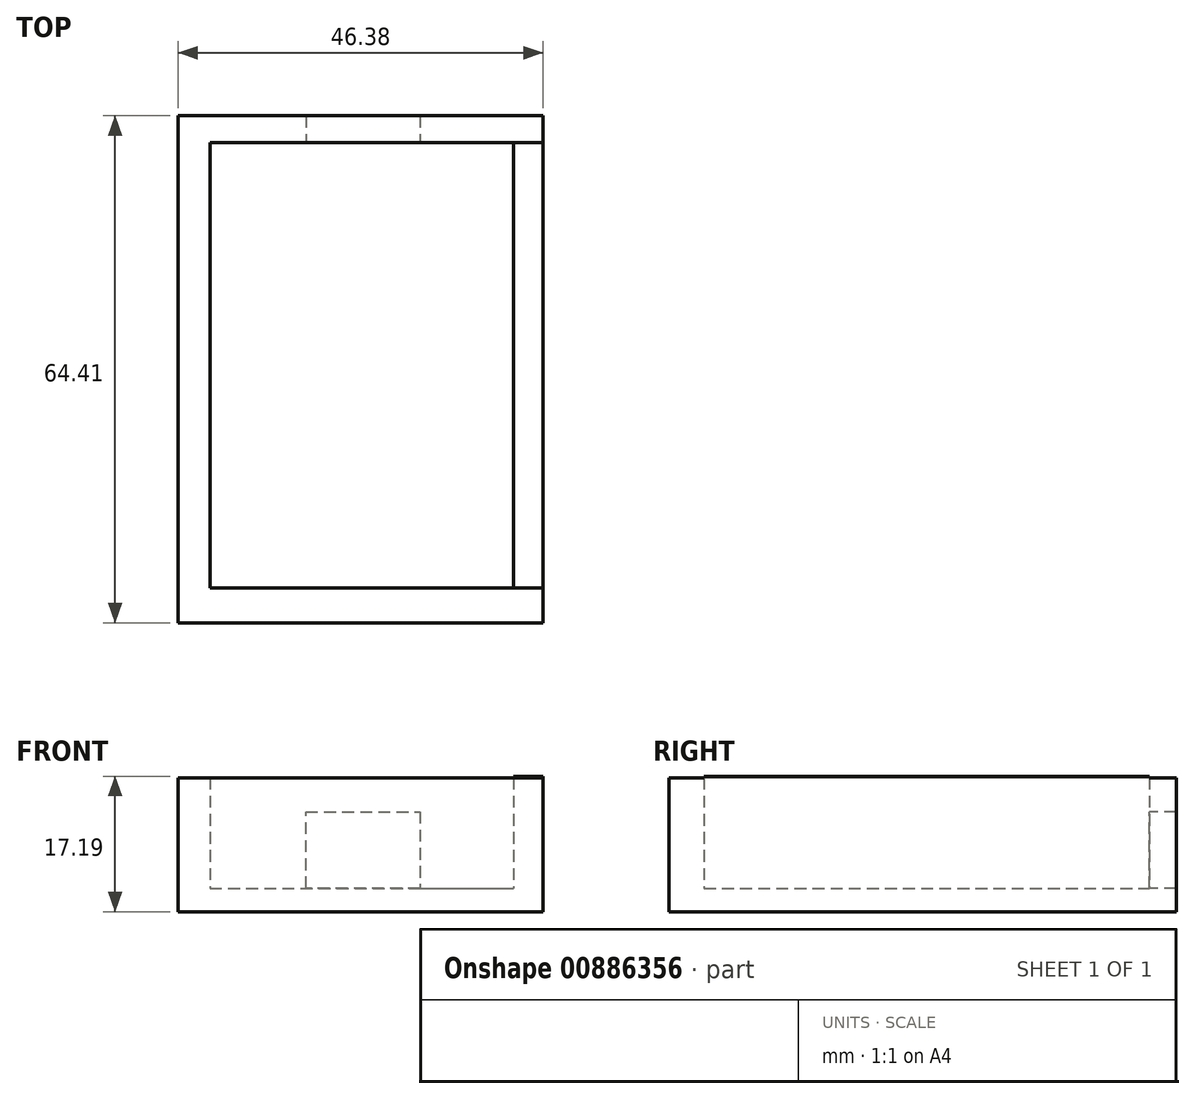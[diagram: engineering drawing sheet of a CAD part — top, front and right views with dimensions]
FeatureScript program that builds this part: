
annotation { "Feature Type Name" : "Feature", "Feature Type Description" : "" }
export const myFeature = defineFeature(function(context is Context, id is Id, definition is map)
    precondition{}
    {
        {
            var Q0;
            Q0=qCreatedBy(makeId("Top.planeOp"),FACE);
            var sketch = newSketch(context, id + "F0", { "sketchPlane" : qUnion([Q0])});
            skLineSegment(sketch, "E0.bottom", {"start": v(0, 0) * mm, "end": v(61.12, 0) * mm});
            skLineSegment(sketch, "E0.top", {"start": v(0, -64.4) * mm, "end": v(61.12, -64.4) * mm});
            skLineSegment(sketch, "E0.left", {"start": v(0, 0) * mm, "end": v(0, -64.4) * mm});
            skLineSegment(sketch, "E0.right", {"start": v(61.12, 0) * mm, "end": v(61.12, -64.4) * mm});
            skLineSegment(sketch, "E1.bottom", {"start": v(2.72, -59.98) * mm, "end": v(57.98, -59.98) * mm});
            skLineSegment(sketch, "E1.top", {"start": v(2.72, -3.43) * mm, "end": v(57.98, -3.43) * mm});
            skLineSegment(sketch, "E1.left", {"start": v(2.72, -59.98) * mm, "end": v(2.72, -3.43) * mm});
            skLineSegment(sketch, "E1.right", {"start": v(57.98, -59.98) * mm, "end": v(57.98, -3.43) * mm});
            skSolve(sketch);
        }
        {
            var Q0;
            Q0=makeQuery(id+"F0.imprint","IMPRINT",FACE,{"disambiguationData":[TD([[makeQuery(id+"F0.imprint","IMPRINT",EDGE,{"derivedFrom":sQuery(id+"F0.wireOp",EDGE,"E0.bottom")}),-1.0]])]});
            extrude(context, id + "F1", {"entities" : qUnion([Q0]), "depth" : 12.7 * mm, "offsetDistance" : 25.4 * mm});
        }
        {
            var Q0;
            Q0=makeQuery(id+"F1.opExtrude","SWEPT_FACE",FACE,{"disambiguationData":[OSD([sQuery(id+"F0.wireOp",EDGE,"E1.top")])]});
            var sketch = newSketch(context, id + "F2", { "sketchPlane" : qUnion([Q0])});
            skLineSegment(sketch, "E2.bottom", {"start": v(2.72, 2.97) * mm, "end": v(57.98, 2.97) * mm});
            skLineSegment(sketch, "E2.top", {"start": v(2.72, 0) * mm, "end": v(57.98, 0) * mm});
            skLineSegment(sketch, "E2.left", {"start": v(2.72, 2.97) * mm, "end": v(2.72, 0) * mm});
            skLineSegment(sketch, "E2.right", {"start": v(57.98, 2.97) * mm, "end": v(57.98, 0) * mm});
            skSolve(sketch);
        }
        {
            var Q0;
            Q0=makeQuery(id+"F2.imprint","IMPRINT",FACE,{"disambiguationData":[TD([[makeQuery(id+"F2.imprint","IMPRINT",EDGE,{"derivedFrom":sQuery(id+"F2.wireOp",EDGE,"E2.bottom")}),-1.0]])]});
            extrude(context, id + "F3", {"entities" : qUnion([Q0]), "operationType" : NewBodyOperationType.ADD, "depth" : 56.9 * mm, "offsetDistance" : 25.4 * mm});
        }
        {
            var Q0;
            Q0=makeQuery(id+"F1.opExtrude","SWEPT_FACE",FACE,{"disambiguationData":[OSD([sQuery(id+"F0.wireOp",EDGE,"E1.top")])]});
            var sketch = newSketch(context, id + "F4", { "sketchPlane" : qUnion([Q0])});
            skLineSegment(sketch, "E3", {"start": v(57.98, 12.7) * mm, "end": v(2.72, 12.7) * mm});
            skLineSegment(sketch, "E4.top", {"start": v(30.35, 2.97) * mm, "end": v(37.6, 2.97) * mm});
            skLineSegment(sketch, "E4.right", {"start": v(37.6, 7.83) * mm, "end": v(37.6, 2.97) * mm});
            skLineSegment(sketch, "E5.top", {"start": v(30.35, 2.97) * mm, "end": v(23.11, 2.97) * mm});
            skLineSegment(sketch, "E5.right", {"start": v(23.11, 7.83) * mm, "end": v(23.11, 2.97) * mm});
            skLineSegment(sketch, "E6.top", {"start": v(30.35, 12.7) * mm, "end": v(23.11, 12.7) * mm});
            skLineSegment(sketch, "E6.right", {"start": v(23.11, 7.83) * mm, "end": v(23.11, 12.7) * mm});
            skLineSegment(sketch, "E7.bottom", {"start": v(30.35, 12.7) * mm, "end": v(37.6, 12.7) * mm});
            skLineSegment(sketch, "E7.right", {"start": v(37.6, 12.7) * mm, "end": v(37.6, 7.83) * mm});
            skPoint(sketch, "E5.left.start.orphan", {"position": v(30.35, 7.83) * mm});
            skPoint(sketch, "E8.start.orphan", {"position": v(57.98, 2.97) * mm});
            skSolve(sketch);
        }
        {
            var Q0;
            Q0=makeQuery(id+"F1.opExtrude","CAP_FACE",FACE,{"disambiguationData":[OSD([sQuery(id+"F0.wireOp",EDGE,"E0.bottom"),sQuery(id+"F0.wireOp",EDGE,"E0.top"),sQuery(id+"F0.wireOp",EDGE,"E0.left"),sQuery(id+"F0.wireOp",EDGE,"E0.right"),sQuery(id+"F0.wireOp",EDGE,"E1.bottom"),sQuery(id+"F0.wireOp",EDGE,"E1.top"),sQuery(id+"F0.wireOp",EDGE,"E1.left"),sQuery(id+"F0.wireOp",EDGE,"E1.right")])],"isStart":false});
            extrude(context, id + "F5", {"entities" : qUnion([Q0]), "operationType" : NewBodyOperationType.ADD, "depth" : 4.32 * mm, "offsetDistance" : 25.4 * mm});
        }
        {
            var Q0;
            Q0=makeQuery(id+"F4.imprint","IMPRINT",FACE,{"disambiguationData":[TD([[makeQuery(id+"F4.imprint","IMPRINT",EDGE,{"derivedFrom":sQuery(id+"F4.wireOp",EDGE,"E4.top")}),1.0]])]});
            extrude(context, id + "F6", {"entities" : qUnion([Q0]), "operationType" : NewBodyOperationType.REMOVE, "oppositeDirection" : true, "depth" : 25.4 * mm, "offsetDistance" : 25.4 * mm});
        }
        {
            var Q0;
            {var subQ0=sQuery(id+"F0.wireOp",EDGE,"E0.right");Q0=makeQuery(id+"F5.boolean.opBoolean","MERGE",FACE,{"derivedFrom":[makeQuery(id+"F1.opExtrude","SWEPT_FACE",FACE,{"disambiguationData":[OSD([subQ0])]}),makeQuery(id+"F5.opExtrude","SWEPT_FACE",FACE,{"disambiguationData":[OSD([subQ0])]})]});}
            extrude(context, id + "F7", {"entities" : qUnion([Q0]), "operationType" : NewBodyOperationType.REMOVE, "oppositeDirection" : true, "depth" : 7.87 * mm, "offsetDistance" : 25.4 * mm});
        }
        {
            var Q0;
            Q0=makeQuery(id+"F6.boolean.opBoolean","MERGE",FACE,{"derivedFrom":[makeQuery(id+"F3.opExtrude","SWEPT_FACE",FACE,{"disambiguationData":[OSD([sQuery(id+"F2.wireOp",EDGE,"E2.bottom")])]})],"fromTools":[makeQuery(id+"F6.opExtrude","SWEPT_FACE",FACE,{"disambiguationData":[OSD([sQuery(id+"F4.wireOp",EDGE,"E4.top"),sQuery(id+"F4.wireOp",EDGE,"E5.top")])]})]});
            var sketch = newSketch(context, id + "F8", { "sketchPlane" : qUnion([Q0])});
            skLineSegment(sketch, "E9.bottom", {"start": v(49.5, -3.43) * mm, "end": v(53.24, -3.43) * mm});
            skLineSegment(sketch, "E9.top", {"start": v(49.5, -59.98) * mm, "end": v(53.24, -59.98) * mm});
            skLineSegment(sketch, "E9.left", {"start": v(49.5, -3.43) * mm, "end": v(49.5, -59.98) * mm});
            skLineSegment(sketch, "E9.right", {"start": v(53.24, -3.43) * mm, "end": v(53.24, -59.98) * mm});
            skSolve(sketch);
        }
        {
            var Q0;
            Q0=makeQuery(id+"F8.imprint","IMPRINT",FACE,{"disambiguationData":[TD([[makeQuery(id+"F8.imprint","IMPRINT",EDGE,{"derivedFrom":sQuery(id+"F8.wireOp",EDGE,"E9.bottom")}),-1.0]])]});
            extrude(context, id + "F9", {"entities" : qUnion([Q0]), "operationType" : NewBodyOperationType.ADD, "depth" : 14.22 * mm, "offsetDistance" : 25.4 * mm});
        }
        {
            var Q0;
            {var subQ0=sQuery(id+"F0.wireOp",EDGE,"E0.left");Q0=makeQuery(id+"F5.boolean.opBoolean","MERGE",FACE,{"derivedFrom":[makeQuery(id+"F1.opExtrude","SWEPT_FACE",FACE,{"disambiguationData":[OSD([subQ0])]}),makeQuery(id+"F5.opExtrude","SWEPT_FACE",FACE,{"disambiguationData":[OSD([subQ0])]})]});}
            extrude(context, id + "F10", {"entities" : qUnion([Q0]), "operationType" : NewBodyOperationType.ADD, "oppositeDirection" : true, "depth" : 10.92 * mm, "offsetDistance" : 25.4 * mm});
        }
        {
            var Q0;
            {var subQ0=sQuery(id+"F0.wireOp",EDGE,"E0.left");Q0=makeQuery(id+"F5.boolean.opBoolean","MERGE",FACE,{"derivedFrom":[makeQuery(id+"F1.opExtrude","SWEPT_FACE",FACE,{"disambiguationData":[OSD([subQ0])]}),makeQuery(id+"F5.opExtrude","SWEPT_FACE",FACE,{"disambiguationData":[OSD([subQ0])]})]});}
            extrude(context, id + "F11", {"entities" : qUnion([Q0]), "operationType" : NewBodyOperationType.REMOVE, "oppositeDirection" : true, "depth" : 6.86 * mm, "offsetDistance" : 25.4 * mm});
        }
    });
